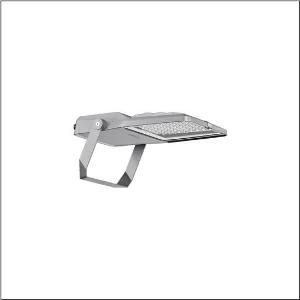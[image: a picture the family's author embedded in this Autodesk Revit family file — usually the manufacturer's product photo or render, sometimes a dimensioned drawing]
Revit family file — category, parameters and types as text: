
# Revit family: floodlight_fl_21_mini___pl52_5xa7773c4d1a_b58d
name_source: partatom
category: Lighting Fixtures
units: mm (PartAtom-declared; Revit-internal decimal feet)

## family parameters
Cut with Voids When Loaded = No
Host = Face
Light Source = No
Part Type = Normal
Room Calculation Point = No
Round Connector Dimension = Use Diameter
Shared = No

## types (1)
- --- (1 x LED, 20360 lm, 163.5 W, 4000K)
    Apparent Load = 163 VA
    CIE Flux Codes = 26 60 98 100 100
    Color Rendering = 70
    Color Temperature = 4000K
    Default Elevation = 1800 mm
    Description = Floodlight FL 21 mini, floodlight, primary light control with lens, of PMMA, primary optical cover: protective disc, of toughened safety glass, transparent, light distribution: PL52, light emission: direct distribution, installation type: surface-mounted, LED, High Power LED, rated luminous flux: 20.360lm, luminous efficacy: 125lm/W, light colour: 740, colour temperature: 4000K, control: Temp-Guard, with terminal, 6-pole, mains connection: 220..240V, AC, 50/60Hz, start of lifetime: 164W, luminaire housing, of diecast aluminium, powder-coated, Siteco® metallic grey (DB 702S), corrosivity category C5 mid according to DIN EN ISO 12944, sealing non-destructively replaceable, mounting bracket, of steel, galvanised, powder-coated, Siteco® metallic grey (DB 702S), ON/OFF, protection rating (complete): IP66, insulation class (complete): insulation class I (protective earthing), certification: CE, ENEC, VDE, protection symbol: D, impact resistance: IK08, permissible operating ambient temperature: -40..+40°C, permissible operating ambient temperature for outdoor applications: -40..+50°C, standard: DIN EN 12944, LABS conformity tested according to VDMA 24364:2018-05, packaging unit: 1 piece

Light Distribution: PL52
    Height = 70 mm
    Lamp = 1 x LED
    Lamp Light Flux = 20360 lm
    Lamp Power = 163.5 W
    Lamp count = 1
    Length = 485 mm
    Luminous efficacy = 125 lm/W
    Manufacturer = Siteco
    ModVariant = No
    Model = 5XA7773C4D1A
    Number of Poles = 1
    OnlyDefault = Yes
    Power Factor = 1
    Product Name = Floodlight FL 21 mini | PL52
    Product group = floodlight | pylon annexe
    ProductGroupID = 6200
    Protection Class = Protection class I
    Protection Degree = IP 66
    RLX_Detail_Level = 1
    RLX_Emergency_Light_Flux = 0 lm
    RLX_Emergency_Type = 0
    RLX_Emergency_Type_DB = No
    RlxData = <blob elided: 94437 chars, md5=f0f3acf6>
    Socket = socket
    Standby Power = 0 W
    System Light Flux = 20360 lm
    System Power = 163 W
    Type Comments = factory setting: luminous flux: 100 % | (ON | - | - | - | - | - | - | -) | 825 mA
    Type Image = l_1006845.jpg
    URL = http://relux.com
    VarID = @adj_096391
    Voltage = 0 V
    Weight = 0.00 kg
    Width = 337 mm

## geometry (parser evidence)
native form markers: Blend x4, Sweep x11
no freeform markers — native parametric forms only
